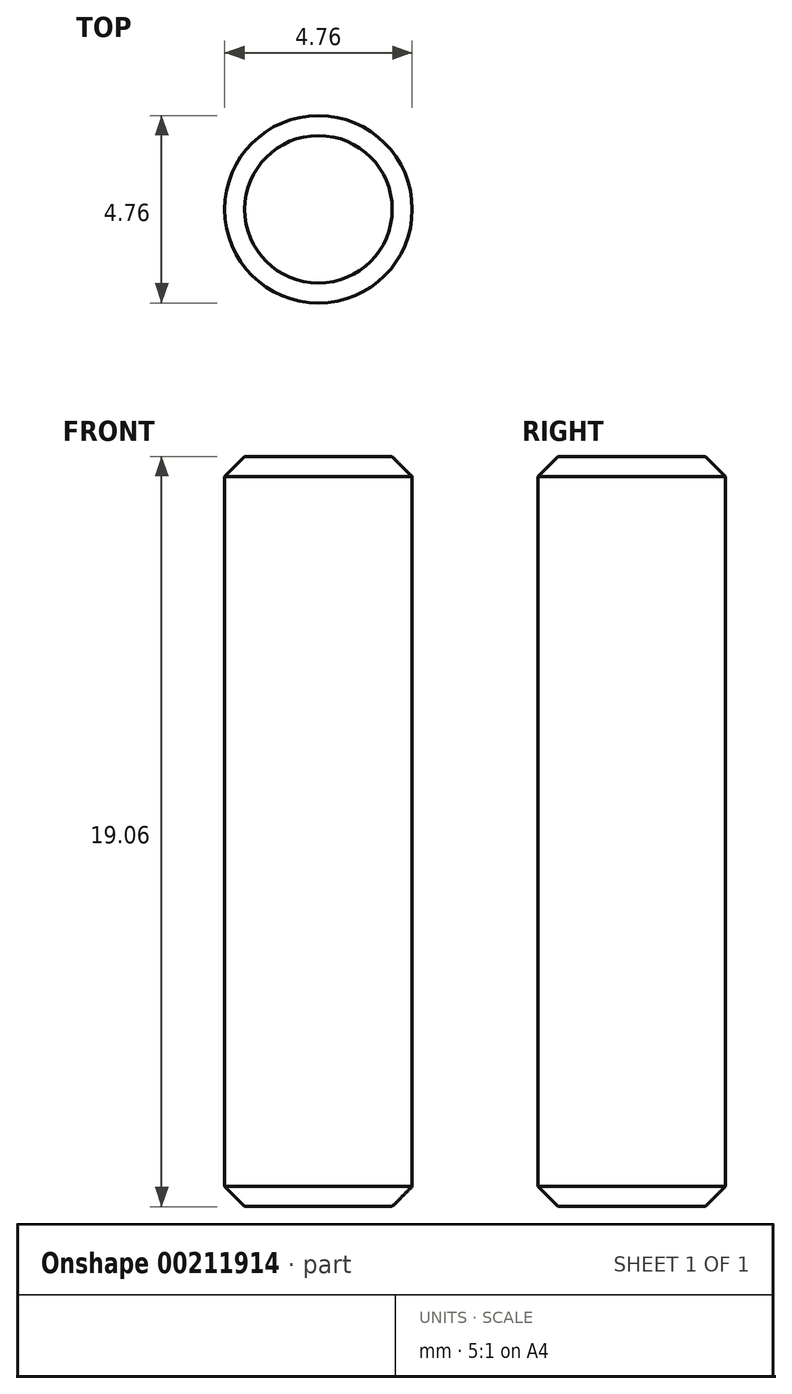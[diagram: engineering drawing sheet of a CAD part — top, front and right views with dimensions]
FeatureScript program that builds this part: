
annotation { "Feature Type Name" : "Feature", "Feature Type Description" : "" }
export const myFeature = defineFeature(function(context is Context, id is Id, definition is map)
    precondition{}
    {
        {
            var Q0;
            Q0=qCreatedBy(makeId("Top.planeOp"),FACE);
            var sketch = newSketch(context, id + "F0", { "sketchPlane" : qUnion([Q0])});
            skCircle(sketch, "E0", {"center": v(0, 0) * mm, "radius": 2.38 * mm});
            skSolve(sketch);
        }
        {
            var Q0;
            Q0=makeQuery(id+"F0.imprint","IMPRINT",FACE,{"disambiguationData":[TD([[makeQuery(id+"F0.imprint","IMPRINT",EDGE,{"derivedFrom":sQuery(id+"F0.wireOp",EDGE,"E0")}),1.0]])]});
            extrude(context, id + "F1", {"entities" : qUnion([Q0]), "endBound" : BoundingType.SYMMETRIC, "depth" : 19.05 * mm});
        }
        {
            var Q0;
            Q0=makeQuery(id+"F1.opExtrude","CAP_EDGE",EDGE,{"disambiguationData":[OSD([sQuery(id+"F0.wireOp",EDGE,"E0")])],"isStart":false});
            var Q1;
            Q1=makeQuery(id+"F1.opExtrude","CAP_EDGE",EDGE,{"disambiguationData":[OSD([sQuery(id+"F0.wireOp",EDGE,"E0")])],"isStart":true});
            chamfer(context, id + "F2", {"entities" : qUnion([Q0, Q1]), "width" : 0.5 * mm, "tangentPropagation" : true});
        }
    });
